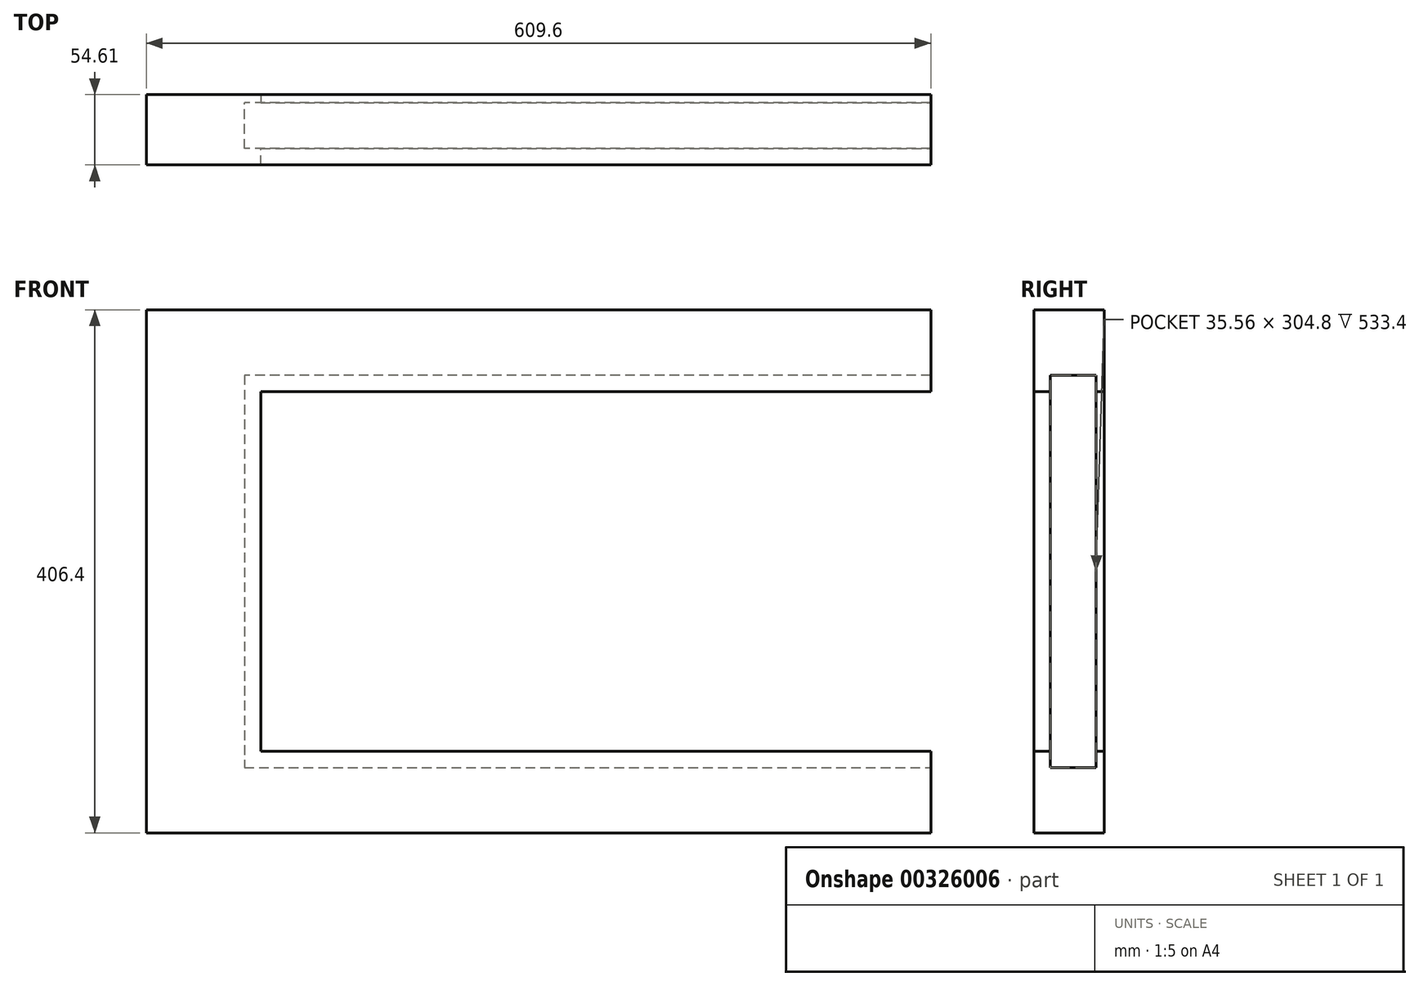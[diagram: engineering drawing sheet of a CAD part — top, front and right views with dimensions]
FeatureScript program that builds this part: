
annotation { "Feature Type Name" : "Feature", "Feature Type Description" : "" }
export const myFeature = defineFeature(function(context is Context, id is Id, definition is map)
    precondition{}
    {
        {
            var Q0;
            Q0=qCreatedBy(makeId("Front.planeOp"),FACE);
            var sketch = newSketch(context, id + "F0", { "sketchPlane" : qUnion([Q0])});
            skLineSegment(sketch, "E0.bottom", {"start": v(254, 152.4) * mm, "end": v(-254, 152.4) * mm});
            skLineSegment(sketch, "E0.top", {"start": v(254, -152.4) * mm, "end": v(-254, -152.4) * mm});
            skLineSegment(sketch, "E0.left", {"start": v(254, 152.4) * mm, "end": v(254, -152.4) * mm});
            skLineSegment(sketch, "E0.right", {"start": v(-254, 152.4) * mm, "end": v(-254, -152.4) * mm});
            skPoint(sketch, "E0.middle", {"position": v(0, 0) * mm});
            skLineSegment(sketch, "E1.bottom", {"start": v(-330.2, -203.2) * mm, "end": v(330.2, -203.2) * mm});
            skLineSegment(sketch, "E1.top", {"start": v(-330.2, 203.2) * mm, "end": v(330.2, 203.2) * mm});
            skLineSegment(sketch, "E1.left", {"start": v(-330.2, -203.2) * mm, "end": v(-330.2, 203.2) * mm});
            skLineSegment(sketch, "E1.right", {"start": v(330.2, -203.2) * mm, "end": v(330.2, 203.2) * mm});
            skLineSegment(sketch, "E2", {"start": v(254, 152.4) * mm, "end": v(330.2, 152.4) * mm});
            skLineSegment(sketch, "E3", {"start": v(254, -152.4) * mm, "end": v(330.2, -152.4) * mm});
            skSolve(sketch);
        }
        {
            var Q0;
            Q0=makeQuery(id+"F0.imprint","IMPRINT",FACE,{"disambiguationData":[TD([[makeQuery(id+"F0.imprint","IMPRINT",EDGE,{"derivedFrom":sQuery(id+"F0.wireOp",EDGE,"E0.bottom")}),-1.0]])]});
            extrude(context, id + "F1", {"entities" : qUnion([Q0]), "depth" : 35.56 * mm});
        }
        {
            var Q0;
            Q0=makeQuery(id+"F1.opExtrude","CAP_FACE",FACE,{"disambiguationData":[OSD([sQuery(id+"F0.wireOp",EDGE,"E0.bottom"),sQuery(id+"F0.wireOp",EDGE,"E0.top"),sQuery(id+"F0.wireOp",EDGE,"E0.right"),sQuery(id+"F0.wireOp",EDGE,"E1.bottom"),sQuery(id+"F0.wireOp",EDGE,"E1.top"),sQuery(id+"F0.wireOp",EDGE,"E1.left"),sQuery(id+"F0.wireOp",EDGE,"E1.right"),sQuery(id+"F0.wireOp",EDGE,"E2"),sQuery(id+"F0.wireOp",EDGE,"E3")])],"isStart":true});
            var sketch = newSketch(context, id + "F2", { "sketchPlane" : qUnion([Q0])});
            skLineSegment(sketch, "E4.bottom", {"start": v(-330.2, 203.2) * mm, "end": v(330.2, 203.2) * mm});
            skLineSegment(sketch, "E4.top", {"start": v(-330.2, -203.2) * mm, "end": v(330.2, -203.2) * mm});
            skLineSegment(sketch, "E4.left", {"start": v(-330.2, 203.2) * mm, "end": v(-330.2, -203.2) * mm});
            skLineSegment(sketch, "E4.right", {"start": v(330.2, 203.2) * mm, "end": v(330.2, -203.2) * mm});
            skLineSegment(sketch, "E5.bottom", {"start": v(241.3, 139.7) * mm, "end": v(-330.2, 139.7) * mm});
            skLineSegment(sketch, "E5.top", {"start": v(241.3, -139.7) * mm, "end": v(-330.2, -139.7) * mm});
            skLineSegment(sketch, "E5.left", {"start": v(241.3, 139.7) * mm, "end": v(241.3, -139.7) * mm});
            skLineSegment(sketch, "E5.right", {"start": v(-330.2, 139.7) * mm, "end": v(-330.2, -139.7) * mm});
            skLineSegment(sketch, "E6.bottom", {"start": v(-330.2, -14.56) * mm, "end": v(-330.2, -14.56) * mm});
            skLineSegment(sketch, "E6.top", {"start": v(-330.2, -18.72) * mm, "end": v(-330.2, -18.72) * mm});
            skLineSegment(sketch, "E6.left", {"start": v(-330.2, -14.56) * mm, "end": v(-330.2, -18.72) * mm});
            skLineSegment(sketch, "E6.right", {"start": v(-330.2, -14.56) * mm, "end": v(-330.2, -18.72) * mm});
            skSolve(sketch);
        }
        {
            var Q0;
            {var subQ0=sQuery(id+"F2.wireOp",EDGE,"E5.bottom");Q0=makeQuery(id+"F2.imprint","IMPRINT",FACE,{"disambiguationData":[TD([[makeQuery(id+"F2.imprint","IMPRINT",EDGE,{"derivedFrom":subQ0}),-1.0]])]});}
            var Q1;
            Q1=makeQuery(id+"F1.opExtrude","CAP_FACE",FACE,{"disambiguationData":[OSD([sQuery(id+"F0.wireOp",EDGE,"E0.bottom"),sQuery(id+"F0.wireOp",EDGE,"E0.top"),sQuery(id+"F0.wireOp",EDGE,"E0.right"),sQuery(id+"F0.wireOp",EDGE,"E1.bottom"),sQuery(id+"F0.wireOp",EDGE,"E1.top"),sQuery(id+"F0.wireOp",EDGE,"E1.left"),sQuery(id+"F0.wireOp",EDGE,"E1.right"),sQuery(id+"F0.wireOp",EDGE,"E2"),sQuery(id+"F0.wireOp",EDGE,"E3")])],"isStart":false});
            var Q2;
            {var subQ4=sQuery(id+"F2.wireOp",EDGE,"E4.bottom");Q2=makeQuery(id+"F2.imprint","IMPRINT",FACE,{"disambiguationData":[TD([[makeQuery(id+"F2.imprint","IMPRINT",EDGE,{"derivedFrom":subQ4}),1.0]])]});}
            extrude(context, id + "F3", {"entities" : qUnion([Q0, Q1, Q2]), "operationType" : NewBodyOperationType.ADD, "depth" : 6.35 * mm});
        }
        {
            var Q0;
            Q0=makeQuery(id+"F1.opExtrude","CAP_FACE",FACE,{"disambiguationData":[OSD([sQuery(id+"F0.wireOp",EDGE,"E0.bottom"),sQuery(id+"F0.wireOp",EDGE,"E0.top"),sQuery(id+"F0.wireOp",EDGE,"E0.right"),sQuery(id+"F0.wireOp",EDGE,"E1.bottom"),sQuery(id+"F0.wireOp",EDGE,"E1.top"),sQuery(id+"F0.wireOp",EDGE,"E1.left"),sQuery(id+"F0.wireOp",EDGE,"E1.right"),sQuery(id+"F0.wireOp",EDGE,"E2"),sQuery(id+"F0.wireOp",EDGE,"E3")])],"isStart":false});
            var sketch = newSketch(context, id + "F4", { "sketchPlane" : qUnion([Q0])});
            skLineSegment(sketch, "E7.bottom", {"start": v(-330.2, 203.2) * mm, "end": v(330.2, 203.2) * mm});
            skLineSegment(sketch, "E7.top", {"start": v(-330.2, -203.2) * mm, "end": v(330.2, -203.2) * mm});
            skLineSegment(sketch, "E7.left", {"start": v(-330.2, 203.2) * mm, "end": v(-330.2, -203.2) * mm});
            skLineSegment(sketch, "E7.right", {"start": v(330.2, 203.2) * mm, "end": v(330.2, -203.2) * mm});
            skLineSegment(sketch, "E8.bottom", {"start": v(-241.3, 139.7) * mm, "end": v(330.2, 139.7) * mm});
            skLineSegment(sketch, "E8.top", {"start": v(-241.3, -139.7) * mm, "end": v(330.2, -139.7) * mm});
            skLineSegment(sketch, "E8.left", {"start": v(-241.3, 139.7) * mm, "end": v(-241.3, -139.7) * mm});
            skLineSegment(sketch, "E8.right", {"start": v(330.2, 139.7) * mm, "end": v(330.2, -139.7) * mm});
            skSolve(sketch);
        }
        {
            var Q0;
            {var subQ3=sQuery(id+"F4.wireOp",EDGE,"E7.bottom");Q0=makeQuery(id+"F4.imprint","IMPRINT",FACE,{"disambiguationData":[TD([[makeQuery(id+"F4.imprint","IMPRINT",EDGE,{"derivedFrom":subQ3}),-1.0]])]});}
            var Q1;
            {var subQ1=sQuery(id+"F4.wireOp",EDGE,"E8.bottom");Q1=makeQuery(id+"F4.imprint","IMPRINT",FACE,{"disambiguationData":[TD([[makeQuery(id+"F4.imprint","IMPRINT",EDGE,{"derivedFrom":subQ1}),1.0]])]});}
            extrude(context, id + "F5", {"entities" : qUnion([Q0, Q1]), "operationType" : NewBodyOperationType.ADD, "depth" : 12.7 * mm});
        }
        {
            var Q0;
            Q0=makeQuery(id+"F3.opExtrude","CAP_FACE",FACE,{"disambiguationData":[OSD([sQuery(id+"F2.wireOp",EDGE,"E4.bottom"),sQuery(id+"F2.wireOp",EDGE,"E4.top"),sQuery(id+"F2.wireOp",EDGE,"E4.left"),sQuery(id+"F2.wireOp",EDGE,"E4.right"),sQuery(id+"F2.wireOp",EDGE,"E5.bottom"),sQuery(id+"F2.wireOp",EDGE,"E5.top"),sQuery(id+"F2.wireOp",EDGE,"E5.left")])],"isStart":false});
            var sketch = newSketch(context, id + "F6", { "sketchPlane" : qUnion([Q0])});
            skLineSegment(sketch, "E9.bottom", {"start": v(-330.2, 203.2) * mm, "end": v(-279.4, 203.2) * mm});
            skLineSegment(sketch, "E9.top", {"start": v(-330.2, -203.2) * mm, "end": v(-279.4, -203.2) * mm});
            skLineSegment(sketch, "E9.left", {"start": v(-330.2, 203.2) * mm, "end": v(-330.2, -203.2) * mm});
            skLineSegment(sketch, "E9.right", {"start": v(-279.4, 203.2) * mm, "end": v(-279.4, -203.2) * mm});
            skSolve(sketch);
        }
        {
            var Q0;
            Q0 = qSketchRegion(id + "F6", true);
            extrude(context, id + "F7", {"entities" : qUnion([Q0]), "operationType" : NewBodyOperationType.REMOVE, "oppositeDirection" : true, "depth" : 162.56 * mm});
        }
    });
